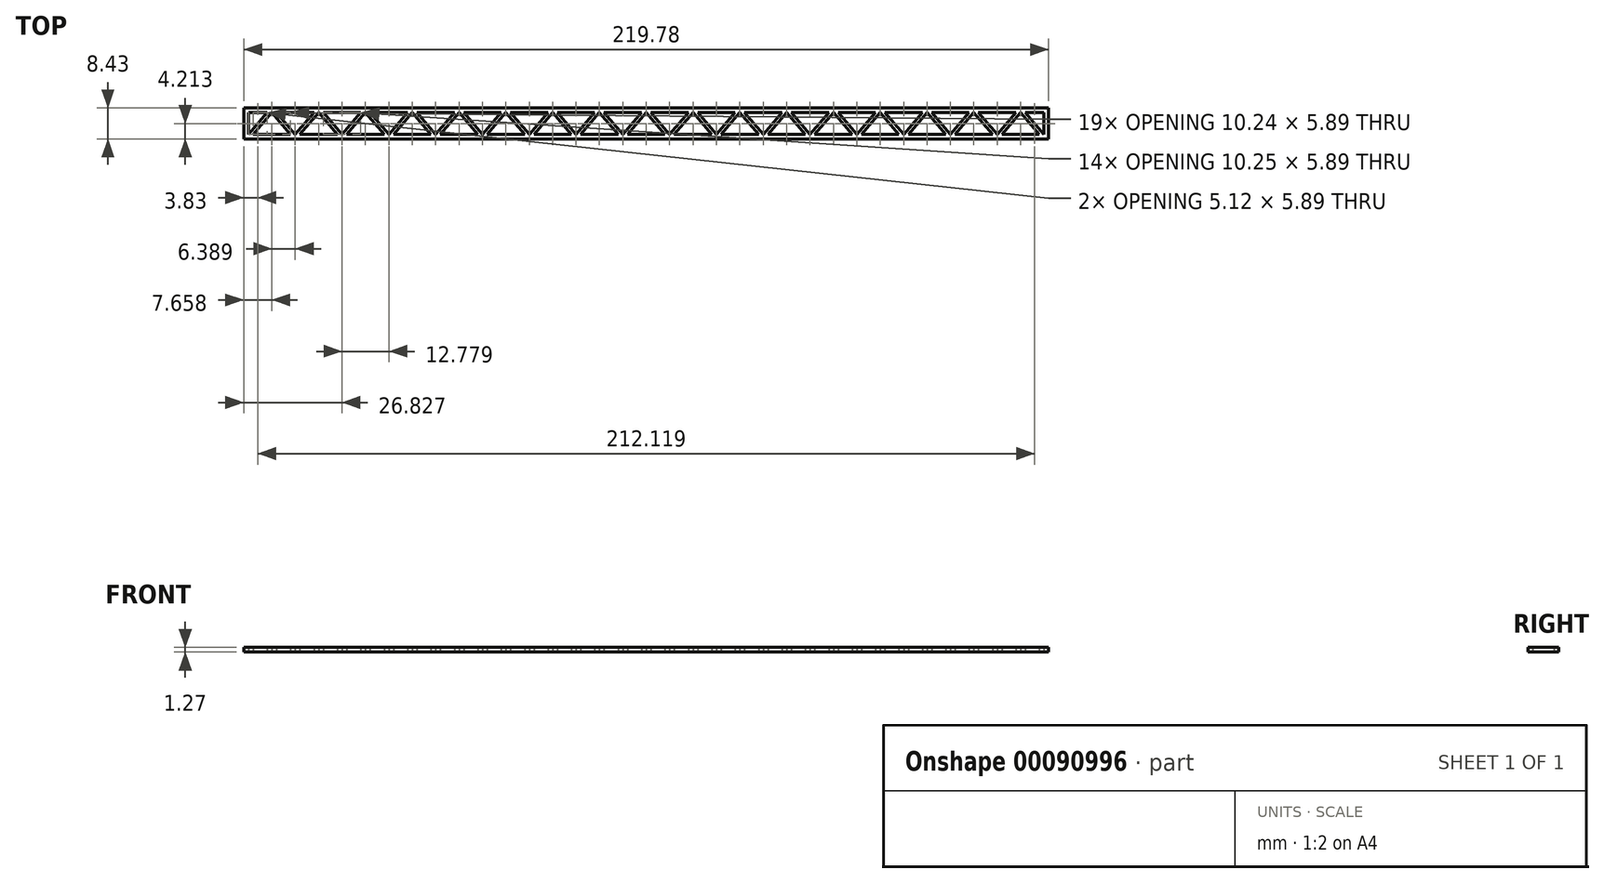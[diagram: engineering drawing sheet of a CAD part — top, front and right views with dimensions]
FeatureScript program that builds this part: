
annotation { "Feature Type Name" : "Feature", "Feature Type Description" : "" }
export const myFeature = defineFeature(function(context is Context, id is Id, definition is map)
    precondition{}
    {
        {
            var Q0;
            Q0=qCreatedBy(makeId("Top.planeOp"),FACE);
            var sketch = newSketch(context, id + "F0", { "sketchPlane" : qUnion([Q0])});
            skLineSegment(sketch, "E0.bottom", {"start": v(-33.8, 43.27) * mm, "end": v(186, 43.27) * mm});
            skLineSegment(sketch, "E0.top", {"start": v(-33.8, 34.84) * mm, "end": v(186, 34.84) * mm});
            skLineSegment(sketch, "E0.left", {"start": v(-33.8, 43.27) * mm, "end": v(-33.8, 34.84) * mm});
            skLineSegment(sketch, "E1.bottom", {"start": v(-32.52, 42) * mm, "end": v(-27.4, 42) * mm});
            skLineSegment(sketch, "E1.top", {"start": v(-31.25, 36.1) * mm, "end": v(-21.01, 36.1) * mm});
            skLineSegment(sketch, "E1.left", {"start": v(-32.52, 42) * mm, "end": v(-32.52, 36.1) * mm});
            skLineSegment(sketch, "E2", {"start": v(-32.52, 36.1) * mm, "end": v(-27.4, 42) * mm});
            skLineSegment(sketch, "E3", {"start": v(-26.13, 42) * mm, "end": v(-31.25, 36.1) * mm});
            skLineSegment(sketch, "E4.MirrorCS", {"start": v(-26.13, 42) * mm, "end": v(-21.01, 36.1) * mm});
            skLineSegment(sketch, "E5.MirrorCS", {"start": v(-19.74, 36.1) * mm, "end": v(-24.86, 42) * mm});
            skLineSegment(sketch, "E6.trimOffspring", {"start": v(-24.86, 42) * mm, "end": v(-14.62, 42) * mm});
            skLineSegment(sketch, "E7.trimOffspring", {"start": v(-18.47, 36.1) * mm, "end": v(-8.23, 36.1) * mm});
            skLineSegment(sketch, "E8.MirrorCS", {"start": v(-19.74, 36.1) * mm, "end": v(-14.62, 42) * mm});
            skLineSegment(sketch, "E9.MirrorCS", {"start": v(-13.35, 42) * mm, "end": v(-18.47, 36.1) * mm});
            skLineSegment(sketch, "E10.MirrorCS", {"start": v(-13.35, 42) * mm, "end": v(-8.23, 36.1) * mm});
            skLineSegment(sketch, "E11.MirrorCS", {"start": v(-6.96, 36.1) * mm, "end": v(-12.09, 42) * mm});
            skLineSegment(sketch, "E12.trimOffspring", {"start": v(-5.7, 36.1) * mm, "end": v(4.55, 36.1) * mm});
            skLineSegment(sketch, "E13.trimOffspring", {"start": v(-12.09, 42) * mm, "end": v(-1.84, 42) * mm});
            skLineSegment(sketch, "E14.MirrorCS", {"start": v(-6.96, 36.1) * mm, "end": v(-1.84, 42) * mm});
            skLineSegment(sketch, "E15.MirrorCS", {"start": v(-0.57, 42) * mm, "end": v(-5.7, 36.1) * mm});
            skLineSegment(sketch, "E16.MirrorCS", {"start": v(-0.57, 42) * mm, "end": v(4.55, 36.1) * mm});
            skLineSegment(sketch, "E17.MirrorCS", {"start": v(5.82, 36.1) * mm, "end": v(0.7, 42) * mm});
            skLineSegment(sketch, "E18.MirrorCS", {"start": v(5.82, 36.1) * mm, "end": v(10.94, 42) * mm});
            skLineSegment(sketch, "E19.MirrorCS", {"start": v(12.2, 42) * mm, "end": v(7.09, 36.1) * mm});
            skLineSegment(sketch, "E20.MirrorCS", {"start": v(12.2, 42) * mm, "end": v(17.32, 36.1) * mm});
            skLineSegment(sketch, "E21.MirrorCS", {"start": v(18.6, 36.1) * mm, "end": v(13.47, 42) * mm});
            skLineSegment(sketch, "E22.trimOffspring", {"start": v(0.7, 42) * mm, "end": v(10.94, 42) * mm});
            skLineSegment(sketch, "E23.trimOffspring", {"start": v(7.09, 36.1) * mm, "end": v(17.32, 36.1) * mm});
            skLineSegment(sketch, "E24.trimOffspring", {"start": v(13.47, 42) * mm, "end": v(23.72, 42) * mm});
            skLineSegment(sketch, "E25.trimOffspring", {"start": v(19.86, 36.1) * mm, "end": v(30.1, 36.1) * mm});
            skLineSegment(sketch, "E26.MirrorCS", {"start": v(18.6, 36.1) * mm, "end": v(23.72, 42) * mm});
            skLineSegment(sketch, "E27.MirrorCS", {"start": v(24.98, 42) * mm, "end": v(19.86, 36.1) * mm});
            skLineSegment(sketch, "E28.MirrorCS", {"start": v(24.98, 42) * mm, "end": v(30.1, 36.1) * mm});
            skLineSegment(sketch, "E29.MirrorCS", {"start": v(31.37, 36.1) * mm, "end": v(26.25, 42) * mm});
            skLineSegment(sketch, "E30.MirrorCS", {"start": v(31.37, 36.1) * mm, "end": v(36.5, 42) * mm});
            skLineSegment(sketch, "E31.MirrorCS", {"start": v(37.76, 42) * mm, "end": v(32.64, 36.1) * mm});
            skLineSegment(sketch, "E32.MirrorCS", {"start": v(37.76, 42) * mm, "end": v(42.88, 36.1) * mm});
            skLineSegment(sketch, "E33.MirrorCS", {"start": v(44.15, 36.1) * mm, "end": v(39.03, 42) * mm});
            skLineSegment(sketch, "E34.MirrorCS", {"start": v(44.15, 36.1) * mm, "end": v(49.28, 42) * mm});
            skLineSegment(sketch, "E35.MirrorCS", {"start": v(50.54, 42) * mm, "end": v(45.42, 36.1) * mm});
            skLineSegment(sketch, "E36.MirrorCS", {"start": v(50.54, 42) * mm, "end": v(55.66, 36.1) * mm});
            skLineSegment(sketch, "E37.MirrorCS", {"start": v(56.93, 36.1) * mm, "end": v(51.8, 42) * mm});
            skLineSegment(sketch, "E38.MirrorCS", {"start": v(56.93, 36.1) * mm, "end": v(62.05, 42) * mm});
            skLineSegment(sketch, "E39.MirrorCS", {"start": v(63.32, 42) * mm, "end": v(58.2, 36.1) * mm});
            skLineSegment(sketch, "E40.MirrorCS", {"start": v(63.32, 42) * mm, "end": v(68.44, 36.1) * mm});
            skLineSegment(sketch, "E41.MirrorCS", {"start": v(69.71, 36.1) * mm, "end": v(64.59, 42) * mm});
            skLineSegment(sketch, "E42.trimOffspring", {"start": v(26.25, 42) * mm, "end": v(36.5, 42) * mm});
            skLineSegment(sketch, "E43.trimOffspring", {"start": v(32.64, 36.1) * mm, "end": v(42.88, 36.1) * mm});
            skLineSegment(sketch, "E44.trimOffspring", {"start": v(39.03, 42) * mm, "end": v(49.28, 42) * mm});
            skLineSegment(sketch, "E45.trimOffspring", {"start": v(45.42, 36.1) * mm, "end": v(55.66, 36.1) * mm});
            skLineSegment(sketch, "E46.trimOffspring", {"start": v(51.8, 42) * mm, "end": v(62.05, 42) * mm});
            skLineSegment(sketch, "E47.trimOffspring", {"start": v(58.2, 36.1) * mm, "end": v(68.44, 36.1) * mm});
            skLineSegment(sketch, "E48.trimOffspring", {"start": v(64.59, 42) * mm, "end": v(74.83, 42) * mm});
            skLineSegment(sketch, "E49.trimOffspring", {"start": v(70.98, 36.1) * mm, "end": v(81.22, 36.1) * mm});
            skLineSegment(sketch, "E50.MirrorCS", {"start": v(69.71, 36.1) * mm, "end": v(74.83, 42) * mm});
            skLineSegment(sketch, "E51.MirrorCS", {"start": v(76.1, 42) * mm, "end": v(70.98, 36.1) * mm});
            skLineSegment(sketch, "E52.MirrorCS", {"start": v(76.1, 42) * mm, "end": v(81.22, 36.1) * mm});
            skLineSegment(sketch, "E53.MirrorCS", {"start": v(82.49, 36.1) * mm, "end": v(77.37, 42) * mm});
            skLineSegment(sketch, "E54.MirrorCS", {"start": v(82.49, 36.1) * mm, "end": v(87.61, 42) * mm});
            skLineSegment(sketch, "E55.MirrorCS", {"start": v(88.88, 42) * mm, "end": v(83.76, 36.1) * mm});
            skLineSegment(sketch, "E56.MirrorCS", {"start": v(88.88, 42) * mm, "end": v(94, 36.1) * mm});
            skLineSegment(sketch, "E57.MirrorCS", {"start": v(95.27, 36.1) * mm, "end": v(90.15, 42) * mm});
            skLineSegment(sketch, "E58.MirrorCS", {"start": v(95.27, 36.1) * mm, "end": v(100.4, 42) * mm});
            skLineSegment(sketch, "E59.MirrorCS", {"start": v(101.66, 42) * mm, "end": v(96.54, 36.1) * mm});
            skLineSegment(sketch, "E60.MirrorCS", {"start": v(101.66, 42) * mm, "end": v(106.78, 36.1) * mm});
            skLineSegment(sketch, "E61.MirrorCS", {"start": v(108.05, 36.1) * mm, "end": v(102.92, 42) * mm});
            skLineSegment(sketch, "E62.MirrorCS", {"start": v(108.05, 36.1) * mm, "end": v(113.17, 42) * mm});
            skLineSegment(sketch, "E63.MirrorCS", {"start": v(114.44, 42) * mm, "end": v(109.32, 36.1) * mm});
            skLineSegment(sketch, "E64.MirrorCS", {"start": v(114.44, 42) * mm, "end": v(119.56, 36.1) * mm});
            skLineSegment(sketch, "E65.MirrorCS", {"start": v(120.83, 36.1) * mm, "end": v(115.7, 42) * mm});
            skLineSegment(sketch, "E66.MirrorCS", {"start": v(120.83, 36.1) * mm, "end": v(125.95, 42) * mm});
            skLineSegment(sketch, "E67.MirrorCS", {"start": v(127.22, 42) * mm, "end": v(122.1, 36.1) * mm});
            skLineSegment(sketch, "E68.MirrorCS", {"start": v(127.22, 42) * mm, "end": v(132.33, 36.1) * mm});
            skLineSegment(sketch, "E69.MirrorCS", {"start": v(133.6, 36.1) * mm, "end": v(128.48, 42) * mm});
            skLineSegment(sketch, "E70.MirrorCS", {"start": v(133.6, 36.1) * mm, "end": v(138.73, 42) * mm});
            skLineSegment(sketch, "E71.MirrorCS", {"start": v(140, 42) * mm, "end": v(134.87, 36.1) * mm});
            skLineSegment(sketch, "E72.MirrorCS", {"start": v(140, 42) * mm, "end": v(145.11, 36.1) * mm});
            skLineSegment(sketch, "E73.MirrorCS", {"start": v(146.38, 36.1) * mm, "end": v(141.26, 42) * mm});
            skLineSegment(sketch, "E74.MirrorCS", {"start": v(146.38, 36.1) * mm, "end": v(151.5, 42) * mm});
            skLineSegment(sketch, "E75.MirrorCS", {"start": v(152.77, 42) * mm, "end": v(147.65, 36.1) * mm});
            skLineSegment(sketch, "E76.MirrorCS", {"start": v(152.77, 42) * mm, "end": v(157.9, 36.1) * mm});
            skLineSegment(sketch, "E77.MirrorCS", {"start": v(159.16, 36.1) * mm, "end": v(154.04, 42) * mm});
            skLineSegment(sketch, "E78.MirrorCS", {"start": v(159.16, 36.1) * mm, "end": v(164.29, 42) * mm});
            skLineSegment(sketch, "E79.MirrorCS", {"start": v(165.55, 42) * mm, "end": v(160.43, 36.1) * mm});
            skLineSegment(sketch, "E80.MirrorCS", {"start": v(165.55, 42) * mm, "end": v(170.67, 36.1) * mm});
            skLineSegment(sketch, "E81.MirrorCS", {"start": v(171.94, 36.1) * mm, "end": v(166.82, 42) * mm});
            skLineSegment(sketch, "E82.MirrorCS", {"start": v(171.94, 36.1) * mm, "end": v(177.06, 42) * mm});
            skLineSegment(sketch, "E83.MirrorCS", {"start": v(178.33, 42) * mm, "end": v(173.21, 36.1) * mm});
            skLineSegment(sketch, "E84.MirrorCS", {"start": v(178.33, 42) * mm, "end": v(183.45, 36.1) * mm});
            skLineSegment(sketch, "E85.MirrorCS", {"start": v(184.72, 36.1) * mm, "end": v(179.6, 42) * mm});
            skLineSegment(sketch, "E86.trimOffspring", {"start": v(179.6, 42) * mm, "end": v(184.72, 42) * mm});
            skLineSegment(sketch, "E87.trimOffspring", {"start": v(173.21, 36.1) * mm, "end": v(183.45, 36.1) * mm});
            skLineSegment(sketch, "E88.trimOffspring", {"start": v(166.82, 42) * mm, "end": v(177.06, 42) * mm});
            skLineSegment(sketch, "E89.trimOffspring", {"start": v(160.43, 36.1) * mm, "end": v(170.67, 36.1) * mm});
            skLineSegment(sketch, "E90.trimOffspring", {"start": v(154.04, 42) * mm, "end": v(164.29, 42) * mm});
            skLineSegment(sketch, "E91.trimOffspring", {"start": v(147.65, 36.1) * mm, "end": v(157.9, 36.1) * mm});
            skLineSegment(sketch, "E92.trimOffspring", {"start": v(141.26, 42) * mm, "end": v(151.5, 42) * mm});
            skLineSegment(sketch, "E93.trimOffspring", {"start": v(134.87, 36.1) * mm, "end": v(145.11, 36.1) * mm});
            skLineSegment(sketch, "E94.trimOffspring", {"start": v(128.48, 42) * mm, "end": v(138.73, 42) * mm});
            skLineSegment(sketch, "E95.trimOffspring", {"start": v(122.1, 36.1) * mm, "end": v(132.33, 36.1) * mm});
            skLineSegment(sketch, "E96.trimOffspring", {"start": v(115.7, 42) * mm, "end": v(125.95, 42) * mm});
            skLineSegment(sketch, "E97.trimOffspring", {"start": v(109.32, 36.1) * mm, "end": v(119.56, 36.1) * mm});
            skLineSegment(sketch, "E98.trimOffspring", {"start": v(102.92, 42) * mm, "end": v(113.17, 42) * mm});
            skLineSegment(sketch, "E99.trimOffspring", {"start": v(96.54, 36.1) * mm, "end": v(106.78, 36.1) * mm});
            skLineSegment(sketch, "E100.trimOffspring", {"start": v(90.15, 42) * mm, "end": v(100.4, 42) * mm});
            skLineSegment(sketch, "E101.trimOffspring", {"start": v(83.76, 36.1) * mm, "end": v(94, 36.1) * mm});
            skLineSegment(sketch, "E102.trimOffspring", {"start": v(77.37, 42) * mm, "end": v(87.61, 42) * mm});
            skLineSegment(sketch, "E103", {"start": v(184.72, 36.1) * mm, "end": v(184.72, 42) * mm});
            skLineSegment(sketch, "E104", {"start": v(186, 36.1) * mm, "end": v(186, 43.27) * mm});
            skLineSegment(sketch, "E105", {"start": v(186, 43.27) * mm, "end": v(186, 34.84) * mm});
            skPoint(sketch, "E106.orphan", {"position": v(189.84, 42) * mm});
            skSolve(sketch);
        }
        {
            var Q0;
            Q0=makeQuery(id+"F0.imprint","IMPRINT",FACE,{"disambiguationData":[TD([[makeQuery(id+"F0.imprint","IMPRINT",EDGE,{"derivedFrom":sQuery(id+"F0.wireOp",EDGE,"E0.bottom")}),-1.0]])]});
            extrude(context, id + "F1", {"entities" : qUnion([Q0]), "depth" : 1.27 * mm});
        }
    });
